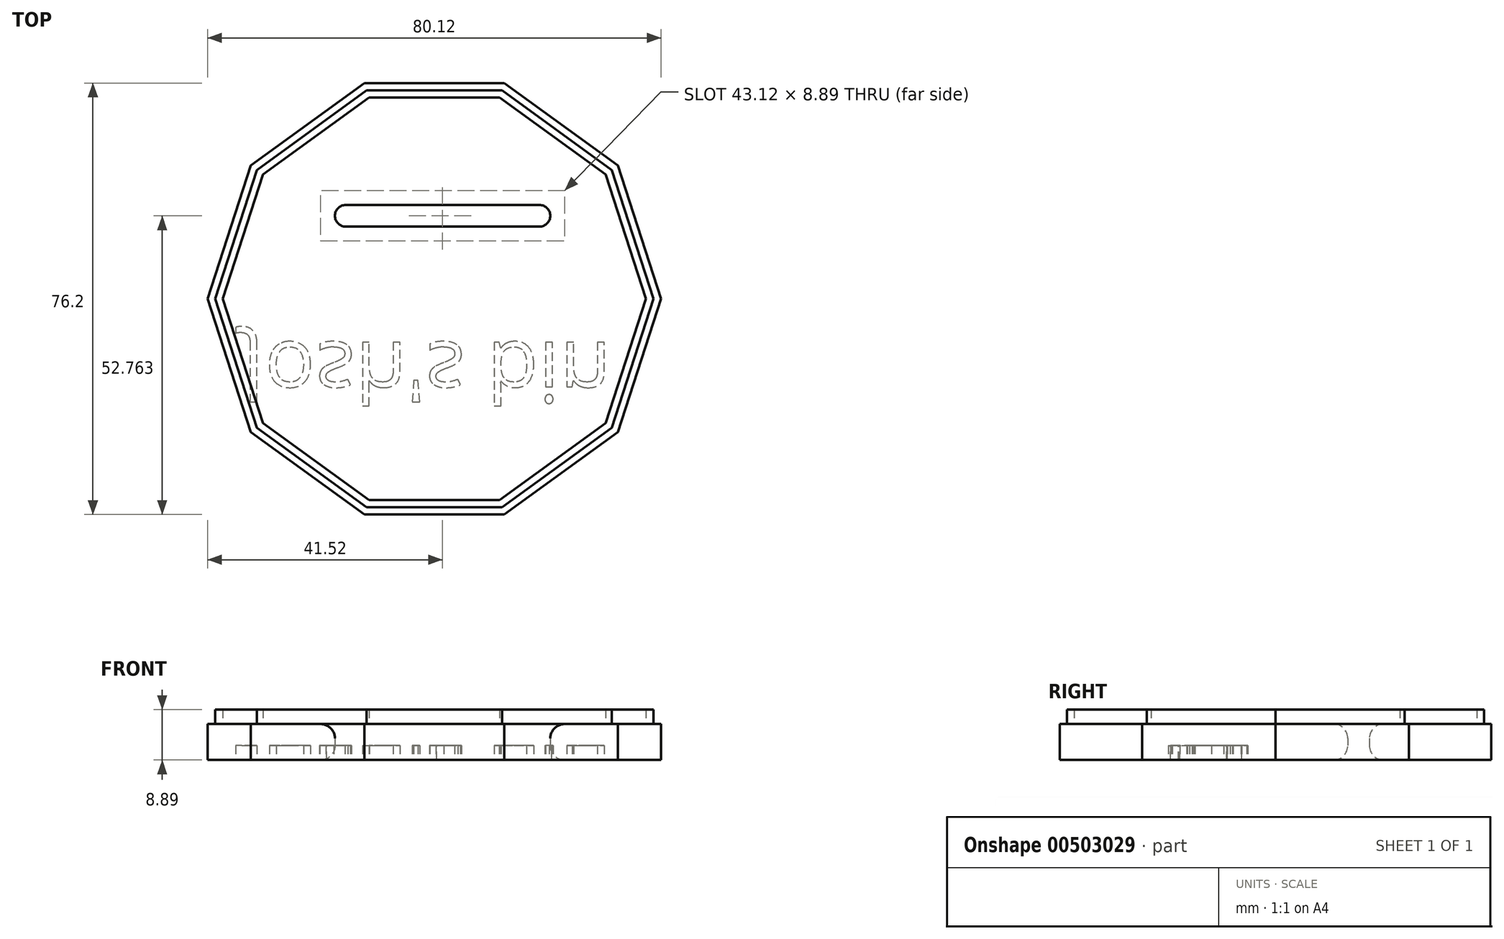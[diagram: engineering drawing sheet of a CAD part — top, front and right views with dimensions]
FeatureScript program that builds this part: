
annotation { "Feature Type Name" : "Feature", "Feature Type Description" : "" }
export const myFeature = defineFeature(function(context is Context, id is Id, definition is map)
    precondition{}
    {
        {
            var Q0;
            Q0=qCreatedBy(makeId("Top.planeOp"),FACE);
            var sketch = newSketch(context, id + "F0", { "sketchPlane" : qUnion([Q0])});
            skCircle(sketch, "E0.cCircle", {"center": v(0, 0) * mm, "radius": 38.1 * mm, "construction": true});
            skLineSegment(sketch, "E0.0", {"start": v(-12.38, 38.1) * mm, "end": v(12.38, 38.1) * mm});
            skLineSegment(sketch, "E0.1", {"start": v(12.38, 38.1) * mm, "end": v(32.4, 23.55) * mm});
            skLineSegment(sketch, "E0.2", {"start": v(32.4, 23.55) * mm, "end": v(40.06, 0) * mm});
            skLineSegment(sketch, "E0.3", {"start": v(40.06, 0) * mm, "end": v(32.4, -23.55) * mm});
            skLineSegment(sketch, "E0.4", {"start": v(32.4, -23.55) * mm, "end": v(12.38, -38.1) * mm});
            skLineSegment(sketch, "E0.5", {"start": v(12.38, -38.1) * mm, "end": v(-12.38, -38.1) * mm});
            skLineSegment(sketch, "E0.6", {"start": v(-12.38, -38.1) * mm, "end": v(-32.4, -23.55) * mm});
            skLineSegment(sketch, "E0.7", {"start": v(-32.4, -23.55) * mm, "end": v(-40.06, 0) * mm});
            skLineSegment(sketch, "E0.8", {"start": v(-40.06, 0) * mm, "end": v(-32.4, 23.55) * mm});
            skLineSegment(sketch, "E0.9", {"start": v(-32.4, 23.55) * mm, "end": v(-12.38, 38.1) * mm});
            skPoint(sketch, "E0.0.midPoint", {"position": v(0, 38.1) * mm});
            skLineSegment(sketch, "E1", {"start": v(-15.65, 14.66) * mm, "end": v(18.57, 14.66) * mm, "construction": true});
            skArc(sketch, "E2.0.startCap", {"start": v(-15.65, 12.76) * mm, "mid": v(-17.56, 14.66) * mm, "end": v(-15.65, 16.57) * mm});
            skArc(sketch, "E2.0.endCap", {"start": v(18.57, 16.57) * mm, "mid": v(20.48, 14.66) * mm, "end": v(18.57, 12.76) * mm});
            skLineSegment(sketch, "E2.0.left", {"start": v(-15.65, 16.57) * mm, "end": v(18.57, 16.57) * mm});
            skLineSegment(sketch, "E2.0.right", {"start": v(-15.65, 12.76) * mm, "end": v(18.57, 12.76) * mm});
            skArc(sketch, "E3.0.startCap", {"start": v(-15.65, 5.14) * mm, "mid": v(-25.18, 14.66) * mm, "end": v(-15.65, 24.19) * mm, "construction": true});
            skArc(sketch, "E3.0.endCap", {"start": v(18.57, 24.19) * mm, "mid": v(28.1, 14.66) * mm, "end": v(18.57, 5.14) * mm, "construction": true});
            skLineSegment(sketch, "E3.0.left", {"start": v(-15.65, 24.19) * mm, "end": v(18.57, 24.19) * mm, "construction": true});
            skLineSegment(sketch, "E3.0.right", {"start": v(-15.65, 5.14) * mm, "end": v(18.57, 5.14) * mm, "construction": true});
            skSolve(sketch);
        }
        {
            var Q0;
            Q0 = qSketchRegion(id + "F0", true);
            extrude(context, id + "F1", {"entities" : qUnion([Q0]), "depth" : 6.35 * mm});
        }
        {
            var Q0;
            Q0=makeQuery(id+"F1.opExtrude","CAP_FACE",FACE,{"disambiguationData":[OSD([sQuery(id+"F0.wireOp",EDGE,"E0.0"),sQuery(id+"F0.wireOp",EDGE,"E0.1"),sQuery(id+"F0.wireOp",EDGE,"E0.2"),sQuery(id+"F0.wireOp",EDGE,"E0.3"),sQuery(id+"F0.wireOp",EDGE,"E0.4"),sQuery(id+"F0.wireOp",EDGE,"E0.5"),sQuery(id+"F0.wireOp",EDGE,"E0.6"),sQuery(id+"F0.wireOp",EDGE,"E0.7"),sQuery(id+"F0.wireOp",EDGE,"E0.8"),sQuery(id+"F0.wireOp",EDGE,"E0.9")])],"isStart":false});
            var sketch = newSketch(context, id + "F2", { "sketchPlane" : qUnion([Q0])});
            skCircle(sketch, "E4.cCircle", {"center": v(0, 0) * mm, "radius": 36.83 * mm, "construction": true});
            skLineSegment(sketch, "E4.0", {"start": v(-31.33, 22.76) * mm, "end": v(-11.97, 36.83) * mm});
            skLineSegment(sketch, "E4.1", {"start": v(-11.97, 36.83) * mm, "end": v(11.97, 36.83) * mm});
            skLineSegment(sketch, "E4.2", {"start": v(11.97, 36.83) * mm, "end": v(31.33, 22.76) * mm});
            skLineSegment(sketch, "E4.3", {"start": v(31.33, 22.76) * mm, "end": v(38.73, 0) * mm});
            skLineSegment(sketch, "E4.4", {"start": v(38.73, 0) * mm, "end": v(31.33, -22.76) * mm});
            skLineSegment(sketch, "E4.5", {"start": v(31.33, -22.76) * mm, "end": v(11.97, -36.83) * mm});
            skLineSegment(sketch, "E4.6", {"start": v(11.97, -36.83) * mm, "end": v(-11.97, -36.83) * mm});
            skLineSegment(sketch, "E4.7", {"start": v(-11.97, -36.83) * mm, "end": v(-31.33, -22.76) * mm});
            skLineSegment(sketch, "E4.8", {"start": v(-31.33, -22.76) * mm, "end": v(-38.73, 0) * mm});
            skLineSegment(sketch, "E4.9", {"start": v(-38.73, 0) * mm, "end": v(-31.33, 22.76) * mm});
            skPoint(sketch, "E4.0.midPoint", {"position": v(-21.65, 29.8) * mm});
            skLineSegment(sketch, "E5", {"start": v(0, 0) * mm, "end": v(-48.6, 0) * mm, "construction": true});
            skCircle(sketch, "E6.cCircle", {"center": v(0, 0) * mm, "radius": 35.56 * mm, "construction": true});
            skLineSegment(sketch, "E6.0", {"start": v(-11.55, 35.56) * mm, "end": v(11.55, 35.56) * mm});
            skLineSegment(sketch, "E6.1", {"start": v(11.55, 35.56) * mm, "end": v(30.25, 21.98) * mm});
            skLineSegment(sketch, "E6.2", {"start": v(30.25, 21.98) * mm, "end": v(37.39, 0) * mm});
            skLineSegment(sketch, "E6.3", {"start": v(37.39, 0) * mm, "end": v(30.25, -21.98) * mm});
            skLineSegment(sketch, "E6.4", {"start": v(30.25, -21.98) * mm, "end": v(11.55, -35.56) * mm});
            skLineSegment(sketch, "E6.5", {"start": v(11.55, -35.56) * mm, "end": v(-11.55, -35.56) * mm});
            skLineSegment(sketch, "E6.6", {"start": v(-11.55, -35.56) * mm, "end": v(-30.25, -21.98) * mm});
            skLineSegment(sketch, "E6.7", {"start": v(-30.25, -21.98) * mm, "end": v(-37.39, 0) * mm});
            skLineSegment(sketch, "E6.8", {"start": v(-37.39, 0) * mm, "end": v(-30.25, 21.98) * mm});
            skLineSegment(sketch, "E6.9", {"start": v(-30.25, 21.98) * mm, "end": v(-11.55, 35.56) * mm});
            skPoint(sketch, "E6.0.midPoint", {"position": v(0, 35.56) * mm});
            skSolve(sketch);
        }
        {
            var Q0;
            Q0 = qSketchRegion(id + "F2", true);
            extrude(context, id + "F3", {"entities" : qUnion([Q0]), "operationType" : NewBodyOperationType.ADD, "depth" : 2.54 * mm});
        }
        {
            var Q0;
            Q0=makeQuery(id+"F1.opExtrude","CAP_FACE",FACE,{"disambiguationData":[OSD([sQuery(id+"F0.wireOp",EDGE,"E0.0"),sQuery(id+"F0.wireOp",EDGE,"E0.1"),sQuery(id+"F0.wireOp",EDGE,"E0.2"),sQuery(id+"F0.wireOp",EDGE,"E0.3"),sQuery(id+"F0.wireOp",EDGE,"E0.4"),sQuery(id+"F0.wireOp",EDGE,"E0.5"),sQuery(id+"F0.wireOp",EDGE,"E0.6"),sQuery(id+"F0.wireOp",EDGE,"E0.7"),sQuery(id+"F0.wireOp",EDGE,"E0.8"),sQuery(id+"F0.wireOp",EDGE,"E0.9")])],"isStart":true});
            var sketch = newSketch(context, id + "F4", { "sketchPlane" : qUnion([Q0])});
            skText(sketch, "E7", { "text": "Josh\'s bin", "fontName": "OpenSans-Regular.ttf"});
            skPoint(sketch, "E7.firstSnap0", {"position": v(-33.93, 30.82) * mm});
            const initialGuessF4  = {"E7": [-0.03393, 0.00765, 1, 0, 0.01066]};
            skSetInitialGuess(sketch, initialGuessF4);
            skSolve(sketch);
        }
        {
            var Q0;
            Q0 = qSketchRegion(id + "F4", true);
            extrude(context, id + "F5", {"entities" : qUnion([Q0]), "operationType" : NewBodyOperationType.REMOVE, "oppositeDirection" : true, "depth" : 2.54 * mm});
        }
        {
            var Q0;
            Q0=qCreatedBy(makeId("Right.planeOp"),FACE);
            var sketch = newSketch(context, id + "F6", { "sketchPlane" : qUnion([Q0])});
            skLineSegment(sketch, "E8", {"start": v(-2.48, 0) * mm, "end": v(-2.48, -10.83) * mm});
            skLineSegment(sketch, "E9", {"start": v(-1.18, 0) * mm, "end": v(-2.48, 0) * mm});
            skArc(sketch, "E10", {"start": v(-2.48, -10.83) * mm, "mid": v(-9.11, -18.77) * mm, "end": v(-1.18, -25.4) * mm});
            skLineSegment(sketch, "E11", {"start": v(-1.18, -25.4) * mm, "end": v(-1.18, -23.54) * mm});
            skLineSegment(sketch, "E12", {"start": v(-1.24, -12.23) * mm, "end": v(-1.18, 0) * mm});
            skLineSegment(sketch, "E13", {"start": v(-1.18, 0) * mm, "end": v(-1.18, -25.4) * mm, "construction": true});
            skLineSegment(sketch, "E14", {"start": v(-1.24, -12.23) * mm, "end": v(-1.18, -23.54) * mm});
            skSolve(sketch);
        }
        {
            var Q0;
            Q0 = qSketchRegion(id + "F6", true);
            var Q1;
            Q1=sQuery(id+"F6.wireOp",EDGE,"E13");
            revolve(context, id + "F7", {"entities" : qUnion([Q0]), "axis" : qUnion([Q1]), "revolveType" : RevolveType.FULL});
        }
        {
            var Q0;
            Q0=makeQuery(id+"F1.opExtrude","CAP_EDGE",EDGE,{"disambiguationData":[OSD([sQuery(id+"F0.wireOp",EDGE,"E2.0.startCap")])],"isStart":true});
            var Q1;
            Q1=makeQuery(id+"F1.opExtrude","CAP_EDGE",EDGE,{"disambiguationData":[OSD([sQuery(id+"F0.wireOp",EDGE,"E2.0.right")])],"isStart":false});
            var Q2;
            Q2=makeQuery(id+"F1.opExtrude","CAP_EDGE",EDGE,{"disambiguationData":[OSD([sQuery(id+"F0.wireOp",EDGE,"E2.0.endCap")])],"isStart":false});
            var Q3;
            Q3=makeQuery(id+"F1.opExtrude","CAP_EDGE",EDGE,{"disambiguationData":[OSD([sQuery(id+"F0.wireOp",EDGE,"E2.0.left")])],"isStart":false});
            var Q4;
            Q4=makeQuery(id+"F1.opExtrude","CAP_EDGE",EDGE,{"disambiguationData":[OSD([sQuery(id+"F0.wireOp",EDGE,"E2.0.startCap")])],"isStart":false});
            fillet(context, id + "F8", {"entities" : qUnion([Q0, Q1, Q2, Q3, Q4]), "radius" : 2.54 * mm, "tangentPropagation" : true, "allowEdgeOverflow" : false});
        }
        {
            var Q0;
            Q0=makeQuery(id+"F7.opRevolve","SWEPT_EDGE",EDGE,{"disambiguationData":[OSD([sQuery(id+"F6.wireOp",EDGE,"E8"),sQuery(id+"F6.wireOp",EDGE,"E10")])]});
            fillet(context, id + "F9", {"entities" : qUnion([Q0]), "radius" : 0.64 * mm, "tangentPropagation" : true, "allowEdgeOverflow" : false});
        }
        {
            var Q0;
            Q0=makeQuery(id+"F1.opExtrude","SWEPT_FACE",FACE,{"disambiguationData":[OSD([sQuery(id+"F0.wireOp",EDGE,"E0.0")])]});
            cPlane(context, id + "F10", {"entities" : qUnion([Q0]), "cplaneType" : CPlaneType.OFFSET, "offset" : 33.02 * mm, "oppositeDirection" : true, "width" : 152.4 * mm, "height" : 152.4 * mm});
        }
        {
            var Q0;
            Q0=qCreatedBy(id+"F10.planeOp",FACE);
            var sketch = newSketch(context, id + "F11", { "sketchPlane" : qUnion([Q0])});
            skPoint(sketch, "E15.0.midPoint", {"position": v(0.08, -22.25) * mm});
            skLineSegment(sketch, "E16", {"start": v(12.9, -22.02) * mm, "end": v(-12.5, -22.02) * mm});
            skLineSegment(sketch, "E17", {"start": v(12.85, -21.26) * mm, "end": v(-12.55, -21.26) * mm});
            skLineSegment(sketch, "E18", {"start": v(-12.55, -21.26) * mm, "end": v(-12.5, -22.02) * mm});
            skLineSegment(sketch, "E19", {"start": v(12.9, -22.02) * mm, "end": v(12.85, -21.26) * mm});
            skPoint(sketch, "E20.0.midPoint", {"position": v(-0.3, -20.17) * mm});
            skPoint(sketch, "E21.0.midPoint", {"position": v(0, -17.85) * mm});
            skLineSegment(sketch, "E22", {"start": v(12.82, -17.62) * mm, "end": v(-12.58, -17.62) * mm});
            skLineSegment(sketch, "E23", {"start": v(12.77, -16.86) * mm, "end": v(-12.63, -16.86) * mm});
            skLineSegment(sketch, "E24", {"start": v(-12.63, -16.86) * mm, "end": v(-12.58, -17.62) * mm});
            skLineSegment(sketch, "E25", {"start": v(12.82, -17.62) * mm, "end": v(12.77, -16.86) * mm});
            skPoint(sketch, "E26.0.midPoint", {"position": v(-0.39, -15.77) * mm});
            skSolve(sketch);
        }
        {
            var Q0;
            Q0 = qSketchRegion(id + "F11", true);
            extrude(context, id + "F12", {"entities" : qUnion([Q0]), "operationType" : NewBodyOperationType.REMOVE, "oppositeDirection" : true, "depth" : 7.62 * mm});
        }
        {
            var Q0;
            Q0=makeQuery(id+"F12.boolean.opBoolean","INTERSECT",EDGE,{"disambiguationData":[OD(1.0)],"derivedFrom":[makeQuery(id+"F7.opRevolve","SWEPT_FACE",FACE,{"disambiguationData":[OSD([sQuery(id+"F6.wireOp",EDGE,"E10")])]}),makeQuery(id+"F12.opExtrude","SWEPT_FACE",FACE,{"disambiguationData":[OSD([sQuery(id+"F11.wireOp",EDGE,"E17")])]})]});
            var Q1;
            Q1=makeQuery(id+"F12.boolean.opBoolean","INTERSECT",EDGE,{"disambiguationData":[OD(0.0)],"derivedFrom":[makeQuery(id+"F7.opRevolve","SWEPT_FACE",FACE,{"disambiguationData":[OSD([sQuery(id+"F6.wireOp",EDGE,"E10")])]}),makeQuery(id+"F12.opExtrude","SWEPT_FACE",FACE,{"disambiguationData":[OSD([sQuery(id+"F11.wireOp",EDGE,"E17")])]})]});
            var Q2;
            Q2=makeQuery(id+"F12.boolean.opBoolean","INTERSECT",EDGE,{"disambiguationData":[OD(0.0)],"derivedFrom":[makeQuery(id+"F7.opRevolve","SWEPT_FACE",FACE,{"disambiguationData":[OSD([sQuery(id+"F6.wireOp",EDGE,"E10")])]}),makeQuery(id+"F12.opExtrude","SWEPT_FACE",FACE,{"disambiguationData":[OSD([sQuery(id+"F11.wireOp",EDGE,"E22")])]})]});
            var Q3;
            Q3=makeQuery(id+"F12.boolean.opBoolean","INTERSECT",EDGE,{"disambiguationData":[OD(1.0)],"derivedFrom":[makeQuery(id+"F7.opRevolve","SWEPT_FACE",FACE,{"disambiguationData":[OSD([sQuery(id+"F6.wireOp",EDGE,"E10")])]}),makeQuery(id+"F12.opExtrude","SWEPT_FACE",FACE,{"disambiguationData":[OSD([sQuery(id+"F11.wireOp",EDGE,"E22")])]})]});
            fillet(context, id + "F13", {"entities" : qUnion([Q0, Q1, Q2, Q3]), "radius" : 1.27 * mm, "tangentPropagation" : true, "allowEdgeOverflow" : false});
        }
    });
